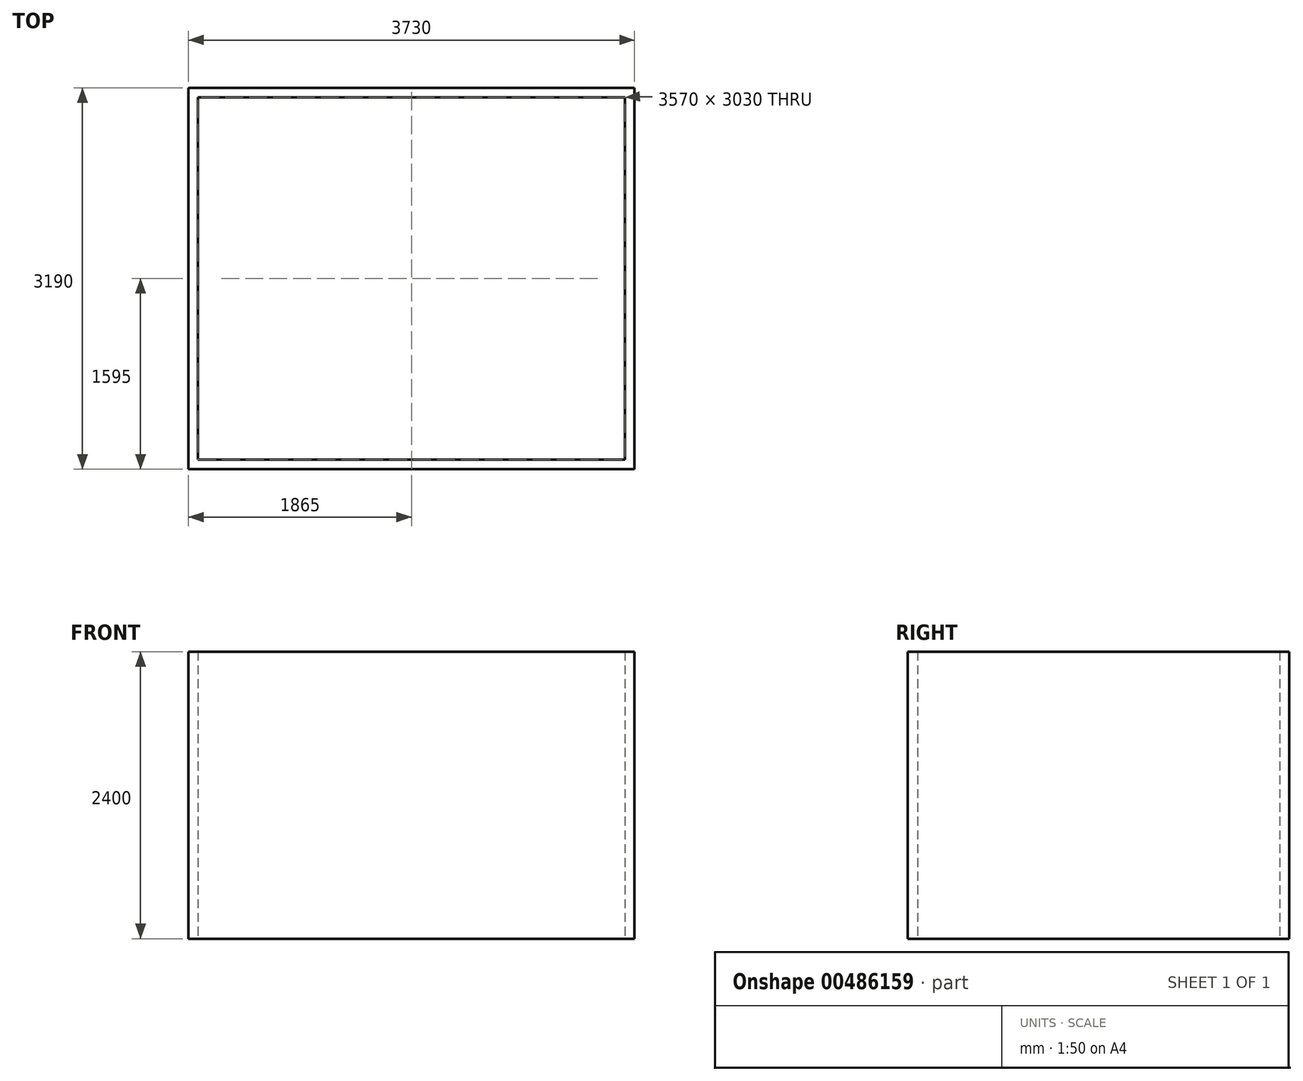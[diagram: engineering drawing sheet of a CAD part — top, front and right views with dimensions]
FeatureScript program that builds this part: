
annotation { "Feature Type Name" : "Feature", "Feature Type Description" : "" }
export const myFeature = defineFeature(function(context is Context, id is Id, definition is map)
    precondition{}
    {
        {
            var Q0;
            Q0=qCreatedBy(makeId("Top.planeOp"),FACE);
            var sketch = newSketch(context, id + "F0", { "sketchPlane" : qUnion([Q0])});
            skLineSegment(sketch, "E0.bottom", {"start": v(-1785, 1515) * mm, "end": v(1785, 1515) * mm});
            skLineSegment(sketch, "E0.top", {"start": v(-1785, -1515) * mm, "end": v(1785, -1515) * mm});
            skLineSegment(sketch, "E0.left", {"start": v(-1785, 1515) * mm, "end": v(-1785, -1515) * mm});
            skLineSegment(sketch, "E0.right", {"start": v(1785, 1515) * mm, "end": v(1785, -1515) * mm});
            skLineSegment(sketch, "E1", {"start": v(-1785, 1515) * mm, "end": v(1785, -1515) * mm, "construction": true});
            skLineSegment(sketch, "E2", {"start": v(1785, 1515) * mm, "end": v(-1785, -1515) * mm, "construction": true});
            skLineSegment(sketch, "E3.bottom", {"start": v(-1865, 1595) * mm, "end": v(1865, 1595) * mm});
            skLineSegment(sketch, "E3.top", {"start": v(-1865, -1595) * mm, "end": v(1865, -1595) * mm});
            skLineSegment(sketch, "E3.left", {"start": v(-1865, 1595) * mm, "end": v(-1865, -1595) * mm});
            skLineSegment(sketch, "E3.right", {"start": v(1865, 1595) * mm, "end": v(1865, -1595) * mm});
            skSolve(sketch);
        }
        {
            var Q0;
            Q0 = qSketchRegion(id + "F0", true);
            extrude(context, id + "F1", {"entities" : qUnion([Q0]), "depth" : 2400 * mm});
        }
    });
